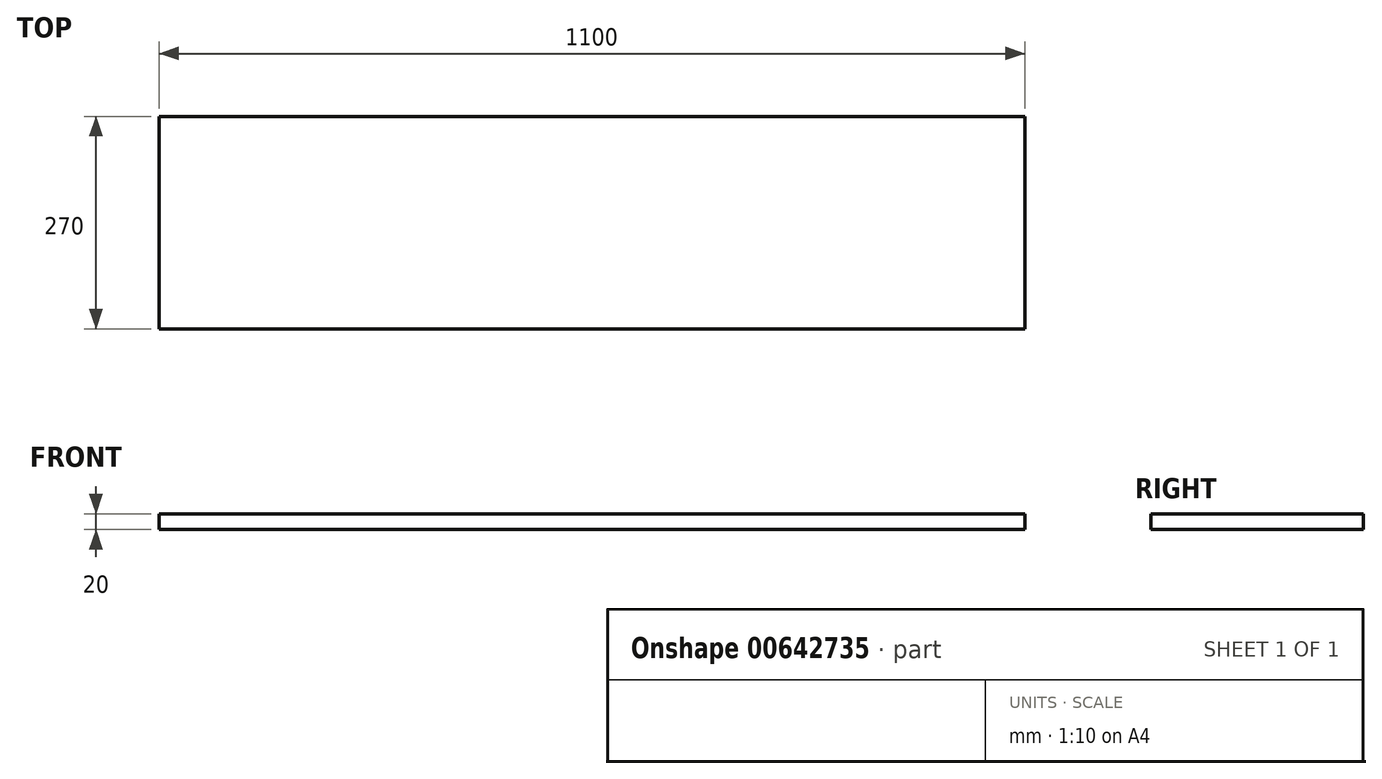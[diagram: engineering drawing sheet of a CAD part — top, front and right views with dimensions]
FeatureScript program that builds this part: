
annotation { "Feature Type Name" : "Feature", "Feature Type Description" : "" }
export const myFeature = defineFeature(function(context is Context, id is Id, definition is map)
    precondition{}
    {
        {
            var Q0;
            Q0=qCreatedBy(makeId("Top.planeOp"),FACE);
            var sketch = newSketch(context, id + "F0", { "sketchPlane" : qUnion([Q0])});
            skLineSegment(sketch, "E0.bottom", {"start": v(0, 0) * mm, "end": v(1100, 0) * mm});
            skLineSegment(sketch, "E0.top", {"start": v(0, 270) * mm, "end": v(1100, 270) * mm});
            skLineSegment(sketch, "E0.left", {"start": v(0, 0) * mm, "end": v(0, 270) * mm});
            skLineSegment(sketch, "E0.right", {"start": v(1100, 0) * mm, "end": v(1100, 270) * mm});
            skSolve(sketch);
        }
        {
            var Q0;
            Q0=qSketchRegion(id+"F0",true);
            extrude(context, id + "F1", {"entities" : qUnion([Q0]), "depth" : 20 * mm, "offsetDistance" : 25 * mm});
        }
    });
